# Revit family: 205_SIL-100-_-900
name_source: partatom
category: Duct Accessories
units: mm (PartAtom-declared; Revit-internal decimal feet)

## family parameters
Always vertical = Yes
Cut with Voids When Loaded = No
Part Type = Breaks Into
Round Connector Dimension = Use Diameter
Shared = No
Work Plane-Based = No

## types (12) — shared parameters
Description = CIRCULAR SILENCER
L1 = 4 mm  [stored 0.0131234 ft]
L2 = 892 mm  [stored 2.92651 ft]
L2D = 900 mm
LL = 450 mm  [stored 1.47638 ft]
Manufacturer = Alnor
QmdConnectorList = 201;D;202;D
SW1 = Yes
URL = http://www.ventilation-alnor.co.uk
magiPartTypeId = 205
magiProductFamilyId = SIL-100-*-900

## per-type parameters (varying)
| type | CD1 | CD2 | D | H2D | R | W2D |
| SIL-100-100-900 | 150 mm  [stored 0.492126 ft] | 151 mm  [stored 0.495407 ft] | 100 mm | 300 mm  [stored 0.984252 ft] | 50 mm  [stored 0.164042 ft] | 300 mm  [stored 0.984252 ft] |
| SIL-100-630-900 | 400 mm | 401 mm | 630 mm | 830 mm | 315 mm | 830 mm |
| SIL-100-500-900 | 400 mm | 401 mm | 500 mm | 700 mm | 250 mm | 700 mm |
| SIL-100-450-900 | 315 mm | 316 mm | 450 mm | 650 mm | 225 mm  [stored 0.738189 ft] | 650 mm |
| SIL-100-400-900 | 300 mm  [stored 0.984252 ft] | 301 mm | 400 mm | 600 mm | 200 mm  [stored 0.656168 ft] | 600 mm |
| SIL-100-355-900 | 280 mm | 281 mm | 355 mm | 555 mm | 178 mm | 555 mm |
| SIL-100-315-900 | 250 mm | 251 mm | 315 mm | 515 mm | 158 mm | 515 mm |
| SIL-100-250-900 | 225 mm  [stored 0.738189 ft] | 226 mm | 250 mm | 450 mm  [stored 1.47638 ft] | 125 mm | 450 mm  [stored 1.47638 ft] |
| SIL-100-200-900 | 200 mm  [stored 0.656168 ft] | 201 mm  [stored 0.659449 ft] | 200 mm | 400 mm | 100 mm  [stored 0.328084 ft] | 400 mm |
| SIL-100-160-900 | 178 mm | 179 mm | 160 mm | 360 mm | 80 mm | 360 mm |
| SIL-100-150-900 | 178 mm | 179 mm | 150 mm | 350 mm | 75 mm | 350 mm |
| SIL-100-125-900 | 158 mm | 159 mm | 125 mm | 325 mm | 63 mm | 325 mm |

note: column(s) folded — value = type name in every type: MC Product Code, magiProductId

note: [stored X ft] marks values corroborated as IEEE doubles in the binary element streams (Revit-internal decimal feet)

## geometry (parser evidence)
native form markers: Blend x4, Sweep x1
no freeform markers — native parametric forms only
